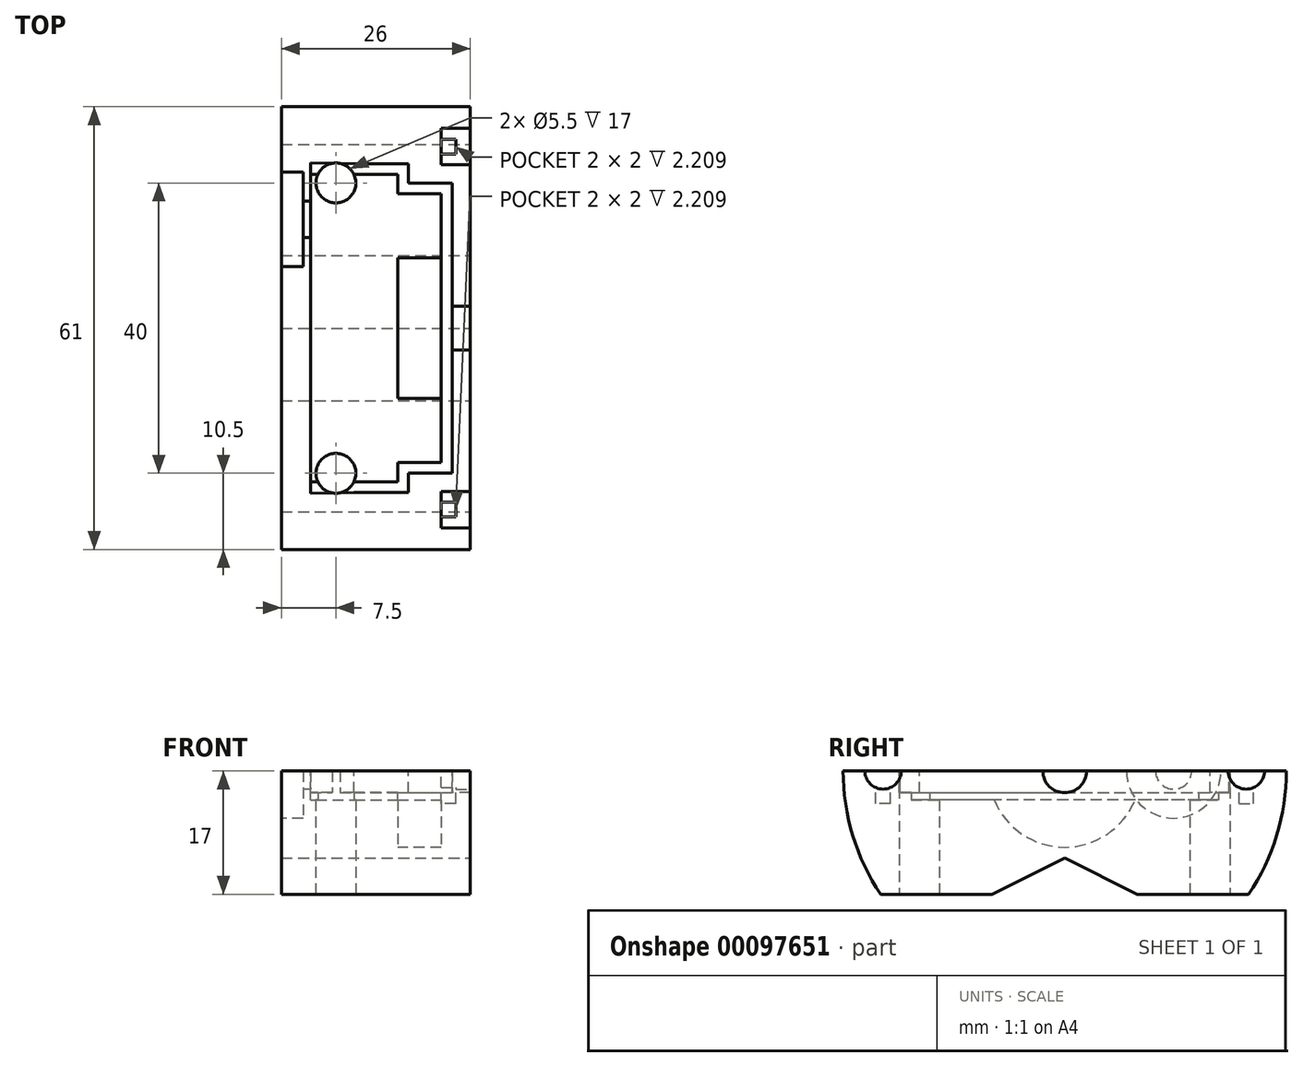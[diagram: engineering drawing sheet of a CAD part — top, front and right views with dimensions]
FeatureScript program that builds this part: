
annotation { "Feature Type Name" : "Feature", "Feature Type Description" : "" }
export const myFeature = defineFeature(function(context is Context, id is Id, definition is map)
    precondition{}
    {
        {
            var Q0;
            Q0=qCreatedBy(makeId("Right.planeOp"),FACE);
            var sketch = newSketch(context, id + "F0", { "sketchPlane" : qUnion([Q0])});
            skArc(sketch, "E0", {"start": v(-30.5, 0) * mm, "mid": v(0, -30.5) * mm, "end": v(30.5, 0) * mm});
            skLineSegment(sketch, "E1.bottom", {"start": v(19.03, -21.15) * mm, "end": v(-19.03, -21.15) * mm});
            skLineSegment(sketch, "E1.left", {"start": v(21.15, -19.03) * mm, "end": v(21.15, 0) * mm});
            skLineSegment(sketch, "E1.right", {"start": v(-21.15, -19.03) * mm, "end": v(-21.15, 0) * mm});
            skLineSegment(sketch, "E2", {"start": v(-30.5, 0) * mm, "end": v(30.5, 0) * mm});
            skPoint(sketch, "E2.endSnap0", {"position": v(21.15, 0) * mm});
            skLineSegment(sketch, "E3", {"start": v(-21.15, -19.03) * mm, "end": v(-19.03, -21.15) * mm});
            skLineSegment(sketch, "E4.MirrorCS", {"start": v(21.15, -19.03) * mm, "end": v(19.03, -21.15) * mm});
            skSolve(sketch);
        }
        {
            var Q0;
            {var subQ0=sQuery(id+"F0.wireOp",EDGE,"E2");var subQ3=sQuery(id+"F0.wireOp",EDGE,"E1.right");var subQ6=makeQuery(id+"F0.imprint","INTERSECT",VERTEX,{"derivedFrom":[subQ3,subQ0]});Q0=makeQuery(id+"F0.imprint","IMPRINT",FACE,{"disambiguationData":[TD([[makeQuery(id+"F0.imprint","IMPRINT",EDGE,{"disambiguationData":[TD([[subQ6,1.0]])],"derivedFrom":subQ3}),1.0]])]});}
            var Q1;
            {var subQ0=sQuery(id+"F0.wireOp",EDGE,"E1.bottom");var subQ5=makeQuery(id+"F0.imprint","INTERSECT",VERTEX,{"derivedFrom":[subQ0,sQuery(id+"F0.wireOp",EDGE,"E3")]});Q1=makeQuery(id+"F0.imprint","IMPRINT",FACE,{"disambiguationData":[TD([[makeQuery(id+"F0.imprint","IMPRINT",EDGE,{"disambiguationData":[TD([[subQ5,1.0]])],"derivedFrom":subQ0}),1.0]])]});}
            var Q2;
            {var subQ0=sQuery(id+"F0.wireOp",EDGE,"E2");var subQ3=sQuery(id+"F0.wireOp",EDGE,"E1.left");var subQ6=makeQuery(id+"F0.imprint","INTERSECT",VERTEX,{"derivedFrom":[subQ3,subQ0]});Q2=makeQuery(id+"F0.imprint","IMPRINT",FACE,{"disambiguationData":[TD([[makeQuery(id+"F0.imprint","IMPRINT",EDGE,{"disambiguationData":[TD([[subQ6,1.0]])],"derivedFrom":subQ3}),-1.0]])]});}
            var Q3;
            {var subQ3=sQuery(id+"F0.wireOp",EDGE,"E4.MirrorCS");Q3=makeQuery(id+"F0.imprint","IMPRINT",FACE,{"disambiguationData":[TD([[makeQuery(id+"F0.imprint","IMPRINT",EDGE,{"derivedFrom":subQ3}),1.0]])]});}
            var Q4;
            {var subQ3=sQuery(id+"F0.wireOp",EDGE,"E3");Q4=makeQuery(id+"F0.imprint","IMPRINT",FACE,{"disambiguationData":[TD([[makeQuery(id+"F0.imprint","IMPRINT",EDGE,{"derivedFrom":subQ3}),-1.0]])]});}
            extrude(context, id + "F1", {"entities" : qUnion([Q0, Q1, Q2, Q3, Q4]), "endBound" : BoundingType.SYMMETRIC, "depth" : 12 * mm});
        }
        {
            var Q0;
            Q0=makeQuery(id+"F1.opExtrude","CAP_FACE",FACE,{"disambiguationData":[OSD([sQuery(id+"F0.wireOp",EDGE,"E0"),sQuery(id+"F0.wireOp",EDGE,"E1.bottom"),sQuery(id+"F0.wireOp",EDGE,"E1.left"),sQuery(id+"F0.wireOp",EDGE,"E1.right"),sQuery(id+"F0.wireOp",EDGE,"E2"),sQuery(id+"F0.wireOp",EDGE,"E3"),sQuery(id+"F0.wireOp",EDGE,"E4.MirrorCS")])],"isStart":false});
            var sketch = newSketch(context, id + "F2", { "sketchPlane" : qUnion([Q0])});
            skArc(sketch, "E5", {"start": v(-30.5, 0) * mm, "mid": v(0, -30.5) * mm, "end": v(30.5, 0) * mm});
            skLineSegment(sketch, "E6", {"start": v(-30.5, 0) * mm, "end": v(30.5, 0) * mm});
            skSolve(sketch);
        }
        {
            var Q0;
            Q0=makeQuery(id+"F2.imprint","IMPRINT",FACE,{"disambiguationData":[TD([[makeQuery(id+"F2.imprint","IMPRINT",EDGE,{"derivedFrom":makeQuery(id+"F1.opExtrude","CAP_EDGE",EDGE,{"disambiguationData":[OSD([sQuery(id+"F0.wireOp",EDGE,"E1.bottom")])],"isStart":false})}),-1.0]])]});
            var Q1;
            {var subQ1=sQuery(id+"F2.wireOp",EDGE,"E5");Q1=makeQuery(id+"F2.imprint","IMPRINT",FACE,{"disambiguationData":[TD([[makeQuery(id+"F2.imprint","IMPRINT",EDGE,{"derivedFrom":subQ1}),1.0]])]});}
            extrude(context, id + "F3", {"entities" : qUnion([Q0, Q1]), "operationType" : NewBodyOperationType.ADD, "depth" : 10 * mm});
        }
        {
            var Q0;
            Q0=makeQuery(id+"F1.opExtrude","CAP_FACE",FACE,{"disambiguationData":[OSD([sQuery(id+"F0.wireOp",EDGE,"E0"),sQuery(id+"F0.wireOp",EDGE,"E1.bottom"),sQuery(id+"F0.wireOp",EDGE,"E1.left"),sQuery(id+"F0.wireOp",EDGE,"E1.right"),sQuery(id+"F0.wireOp",EDGE,"E2"),sQuery(id+"F0.wireOp",EDGE,"E3"),sQuery(id+"F0.wireOp",EDGE,"E4.MirrorCS")])],"isStart":true});
            var sketch = newSketch(context, id + "F4", { "sketchPlane" : qUnion([Q0])});
            skArc(sketch, "E7", {"start": v(-30.5, 0) * mm, "mid": v(0, -30.5) * mm, "end": v(30.5, 0) * mm});
            skLineSegment(sketch, "E8", {"start": v(-30.5, 0) * mm, "end": v(30.5, 0) * mm});
            skSolve(sketch);
        }
        {
            var Q0;
            Q0=makeQuery(id+"F4.imprint","IMPRINT",FACE,{"disambiguationData":[TD([[makeQuery(id+"F4.imprint","IMPRINT",EDGE,{"derivedFrom":makeQuery(id+"F1.opExtrude","CAP_EDGE",EDGE,{"disambiguationData":[OSD([sQuery(id+"F0.wireOp",EDGE,"E1.bottom")])],"isStart":true})}),1.0]])]});
            var Q1;
            {var subQ1=sQuery(id+"F4.wireOp",EDGE,"E7");Q1=makeQuery(id+"F4.imprint","IMPRINT",FACE,{"disambiguationData":[TD([[makeQuery(id+"F4.imprint","IMPRINT",EDGE,{"derivedFrom":subQ1}),-1.0]])]});}
            extrude(context, id + "F5", {"entities" : qUnion([Q0, Q1]), "operationType" : NewBodyOperationType.ADD, "depth" : 4 * mm});
        }
        {
            var Q0;
            {var subQ0=sQuery(id+"F0.wireOp",EDGE,"E2");var subQ1=sQuery(id+"F0.wireOp",EDGE,"E0");Q0=makeQuery(id+"F5.boolean.opBoolean","MERGE",FACE,{"derivedFrom":[makeQuery(id+"F3.boolean.opBoolean","MERGE",FACE,{"derivedFrom":[makeQuery(id+"F1.opExtrude","SWEPT_FACE",FACE,{"disambiguationData":[OSD([subQ0]),TDD([makeQuery(id+"F0.imprint","IMPRINT",EDGE,{"disambiguationData":[TD([[makeQuery(id+"F0.imprint","INTERSECT",VERTEX,{"disambiguationData":[OD(0.0)],"derivedFrom":[subQ1,subQ0]}),-1.0]])],"derivedFrom":subQ0})])]}),makeQuery(id+"F1.opExtrude","SWEPT_FACE",FACE,{"disambiguationData":[OSD([subQ0]),TDD([makeQuery(id+"F0.imprint","IMPRINT",EDGE,{"disambiguationData":[TD([[makeQuery(id+"F0.imprint","INTERSECT",VERTEX,{"disambiguationData":[OD(1.0)],"derivedFrom":[subQ1,subQ0]}),1.0]])],"derivedFrom":subQ0})])]}),makeQuery(id+"F3.opExtrude","SWEPT_FACE",FACE,{"disambiguationData":[OSD([sQuery(id+"F2.wireOp",EDGE,"E6")])]})]}),makeQuery(id+"F5.opExtrude","SWEPT_FACE",FACE,{"disambiguationData":[OSD([sQuery(id+"F4.wireOp",EDGE,"E8")])]})]});}
            var sketch = newSketch(context, id + "F6", { "sketchPlane" : qUnion([Q0])});
            skLineSegment(sketch, "E9.bottom", {"start": v(6, 0) * mm, "end": v(12, 0) * mm});
            skLineSegment(sketch, "E9.top", {"start": v(6, 10.5) * mm, "end": v(12, 10.5) * mm});
            skLineSegment(sketch, "E9.left", {"start": v(6, 0) * mm, "end": v(6, 10.5) * mm});
            skLineSegment(sketch, "E9.right", {"start": v(12, 0) * mm, "end": v(12, 10.5) * mm});
            skLineSegment(sketch, "E10.bottom", {"start": v(16, 0) * mm, "end": v(12, 0) * mm});
            skLineSegment(sketch, "E10.top", {"start": v(16, 3) * mm, "end": v(12, 3) * mm});
            skLineSegment(sketch, "E10.left", {"start": v(16, 0) * mm, "end": v(16, 3) * mm});
            skLineSegment(sketch, "E10.right", {"start": v(12, 0) * mm, "end": v(12, 3) * mm});
            skLineSegment(sketch, "E11.bottom", {"start": v(12, -22.5) * mm, "end": v(16, -22.5) * mm});
            skLineSegment(sketch, "E11.top", {"start": v(12, -27.5) * mm, "end": v(16, -27.5) * mm});
            skLineSegment(sketch, "E11.left", {"start": v(12, -22.5) * mm, "end": v(12, -27.5) * mm});
            skLineSegment(sketch, "E11.right", {"start": v(16, -22.5) * mm, "end": v(16, -27.5) * mm});
            skLineSegment(sketch, "E12.MirrorCS", {"start": v(12, 22.5) * mm, "end": v(12, 27.5) * mm});
            skLineSegment(sketch, "E13.MirrorCS", {"start": v(12, 22.5) * mm, "end": v(16, 22.5) * mm});
            skLineSegment(sketch, "E14.MirrorCS", {"start": v(12, 27.5) * mm, "end": v(16, 27.5) * mm});
            skLineSegment(sketch, "E15.MirrorCS", {"start": v(16, 22.5) * mm, "end": v(16, 27.5) * mm});
            skLineSegment(sketch, "E16", {"start": v(12, -25) * mm, "end": v(16, -25) * mm});
            skLineSegment(sketch, "E17.MirrorCS", {"start": v(12, 25) * mm, "end": v(16, 25) * mm});
            skSolve(sketch);
        }
        {
            var Q0;
            Q0=makeQuery(id+"F6.imprint","IMPRINT",FACE,{"disambiguationData":[TD([[makeQuery(id+"F6.imprint","IMPRINT",EDGE,{"derivedFrom":sQuery(id+"F6.wireOp",EDGE,"E9.bottom")}),1.0]])]});
            var Q1;
            Q1=makeQuery(id+"F6.imprint","IMPRINT",FACE,{"disambiguationData":[TD([[makeQuery(id+"F6.imprint","IMPRINT",EDGE,{"derivedFrom":sQuery(id+"F6.wireOp",EDGE,"E10.bottom")}),-1.0]])]});
            var Q2;
            Q2=sQuery(id+"F6.wireOp",EDGE,"E9.bottom");
            revolve(context, id + "F7", {"operationType" : NewBodyOperationType.REMOVE, "entities" : qUnion([Q0, Q1]), "axis" : qUnion([Q2]), "revolveType" : RevolveType.FULL});
        }
        {
            var Q0;
            {var subQ0=sQuery(id+"F6.wireOp",EDGE,"E11.top");Q0=makeQuery(id+"F6.imprint","IMPRINT",FACE,{"disambiguationData":[TD([[makeQuery(id+"F6.imprint","IMPRINT",EDGE,{"derivedFrom":subQ0}),1.0]])]});}
            var Q1;
            Q1=sQuery(id+"F6.wireOp",EDGE,"E16");
            revolve(context, id + "F8", {"operationType" : NewBodyOperationType.REMOVE, "entities" : qUnion([Q0]), "axis" : qUnion([Q1]), "revolveType" : RevolveType.FULL, "oppositeDirection" : true});
        }
        {
            var Q0;
            {var subQ0=sQuery(id+"F6.wireOp",EDGE,"E13.MirrorCS");Q0=makeQuery(id+"F6.imprint","IMPRINT",FACE,{"disambiguationData":[TD([[makeQuery(id+"F6.imprint","IMPRINT",EDGE,{"derivedFrom":subQ0}),1.0]])]});}
            var Q1;
            Q1=sQuery(id+"F6.wireOp",EDGE,"E17.MirrorCS");
            revolve(context, id + "F9", {"operationType" : NewBodyOperationType.REMOVE, "entities" : qUnion([Q0]), "axis" : qUnion([Q1]), "revolveType" : RevolveType.FULL, "oppositeDirection" : true});
        }
        {
            var Q0;
            {var subQ16=sQuery(id+"F6.wireOp",EDGE,"E9.bottom");Q0=makeQuery(id+"F6.imprint","IMPRINT",FACE,{"disambiguationData":[TD([[makeQuery(id+"F6.imprint","IMPRINT",EDGE,{"derivedFrom":subQ16}),-1.0]])]});}
            var sketch = newSketch(context, id + "F10", { "sketchPlane" : qUnion([Q0])});
            skLineSegment(sketch, "E18.bottom", {"start": v(14, -26) * mm, "end": v(12, -26) * mm});
            skLineSegment(sketch, "E18.top", {"start": v(14, -24) * mm, "end": v(12, -24) * mm});
            skLineSegment(sketch, "E18.left", {"start": v(14, -26) * mm, "end": v(14, -24) * mm});
            skPoint(sketch, "E18.middle", {"position": v(12, -25) * mm});
            skLineSegment(sketch, "E19", {"start": v(12, -24) * mm, "end": v(12, -26) * mm});
            skPoint(sketch, "E18.right.end.orphan", {"position": v(10, -24) * mm});
            skPoint(sketch, "E20.orphan", {"position": v(10, -26) * mm});
            skLineSegment(sketch, "E21.MirrorCS", {"start": v(14, 24) * mm, "end": v(12, 24) * mm});
            skLineSegment(sketch, "E22.MirrorCS", {"start": v(14, 26) * mm, "end": v(14, 24) * mm});
            skLineSegment(sketch, "E23.MirrorCS", {"start": v(14, 26) * mm, "end": v(12, 26) * mm});
            skLineSegment(sketch, "E24.MirrorCS", {"start": v(12, 24) * mm, "end": v(12, 26) * mm});
            skSolve(sketch);
        }
        {
            var Q0;
            {var subQ5=sQuery(id+"F10.wireOp",EDGE,"E18.bottom");Q0=makeQuery(id+"F10.imprint","IMPRINT",FACE,{"disambiguationData":[TD([[makeQuery(id+"F10.imprint","IMPRINT",EDGE,{"derivedFrom":subQ5}),-1.0]])]});}
            var Q1;
            {var subQ2=sQuery(id+"F10.wireOp",EDGE,"E21.MirrorCS");Q1=makeQuery(id+"F10.imprint","IMPRINT",FACE,{"disambiguationData":[TD([[makeQuery(id+"F10.imprint","IMPRINT",EDGE,{"derivedFrom":subQ2}),-1.0]])]});}
            extrude(context, id + "F11", {"entities" : qUnion([Q0, Q1]), "operationType" : NewBodyOperationType.REMOVE, "oppositeDirection" : true, "depth" : 4.5 * mm});
        }
        {
            var Q0;
            {var subQ0=sQuery(id+"F0.wireOp",EDGE,"E2");var subQ1=sQuery(id+"F0.wireOp",EDGE,"E0");Q0=makeQuery(id+"F5.boolean.opBoolean","MERGE",FACE,{"derivedFrom":[makeQuery(id+"F3.boolean.opBoolean","MERGE",FACE,{"derivedFrom":[makeQuery(id+"F1.opExtrude","SWEPT_FACE",FACE,{"disambiguationData":[OSD([subQ0]),TDD([makeQuery(id+"F0.imprint","IMPRINT",EDGE,{"disambiguationData":[TD([[makeQuery(id+"F0.imprint","INTERSECT",VERTEX,{"disambiguationData":[OD(0.0)],"derivedFrom":[subQ1,subQ0]}),-1.0]])],"derivedFrom":subQ0})])]}),makeQuery(id+"F1.opExtrude","SWEPT_FACE",FACE,{"disambiguationData":[OSD([subQ0]),TDD([makeQuery(id+"F0.imprint","IMPRINT",EDGE,{"disambiguationData":[TD([[makeQuery(id+"F0.imprint","INTERSECT",VERTEX,{"disambiguationData":[OD(1.0)],"derivedFrom":[subQ1,subQ0]}),1.0]])],"derivedFrom":subQ0})])]}),makeQuery(id+"F3.opExtrude","SWEPT_FACE",FACE,{"disambiguationData":[OSD([sQuery(id+"F2.wireOp",EDGE,"E6")])]})]}),makeQuery(id+"F5.opExtrude","SWEPT_FACE",FACE,{"disambiguationData":[OSD([sQuery(id+"F4.wireOp",EDGE,"E8")])]})]});}
            var sketch = newSketch(context, id + "F12", { "sketchPlane" : qUnion([Q0])});
            skLineSegment(sketch, "E25.bottom", {"start": v(6, 18.5) * mm, "end": v(12, 18.5) * mm});
            skLineSegment(sketch, "E25.top", {"start": v(6, -18.5) * mm, "end": v(12, -18.5) * mm});
            skLineSegment(sketch, "E25.left", {"start": v(6, 18.5) * mm, "end": v(6, -18.5) * mm});
            skLineSegment(sketch, "E25.right", {"start": v(12, 18.5) * mm, "end": v(12, -18.5) * mm});
            skPoint(sketch, "E26", {"position": v(9, 15.5) * mm});
            skPoint(sketch, "E27.MirrorP", {"position": v(9, -15.5) * mm});
            skSolve(sketch);
        }
        {
            var Q0;
            {var subQ7=sQuery(id+"F12.wireOp",EDGE,"E25.bottom");Q0=makeQuery(id+"F12.imprint","IMPRINT",FACE,{"disambiguationData":[TD([[makeQuery(id+"F12.imprint","IMPRINT",EDGE,{"derivedFrom":subQ7}),-1.0]])]});}
            var Q1;
            {var subQ4=sQuery(id+"F12.wireOp",EDGE,"E25.top");Q1=makeQuery(id+"F12.imprint","IMPRINT",FACE,{"disambiguationData":[TD([[makeQuery(id+"F12.imprint","IMPRINT",EDGE,{"derivedFrom":subQ4}),1.0]])]});}
            var Q2;
            {var subQ0=sQuery(id+"F12.wireOp",EDGE,"E25.left");var subQ1=makeQuery(id+"F7.opRevolve","SWEPT_FACE",FACE,{"disambiguationData":[OSD([sQuery(id+"F6.wireOp",EDGE,"E9.top")])]});var subQ2=sQuery(id+"F0.wireOp",EDGE,"E2");var subQ3=sQuery(id+"F0.wireOp",EDGE,"E0");var subQ4=makeQuery(id+"F5.boolean.opBoolean","MERGE",FACE,{"derivedFrom":[makeQuery(id+"F3.boolean.opBoolean","MERGE",FACE,{"derivedFrom":[makeQuery(id+"F1.opExtrude","SWEPT_FACE",FACE,{"disambiguationData":[OSD([subQ2]),TDD([makeQuery(id+"F0.imprint","IMPRINT",EDGE,{"disambiguationData":[TD([[makeQuery(id+"F0.imprint","INTERSECT",VERTEX,{"disambiguationData":[OD(0.0)],"derivedFrom":[subQ3,subQ2]}),-1.0]])],"derivedFrom":subQ2})])]}),makeQuery(id+"F1.opExtrude","SWEPT_FACE",FACE,{"disambiguationData":[OSD([subQ2]),TDD([makeQuery(id+"F0.imprint","IMPRINT",EDGE,{"disambiguationData":[TD([[makeQuery(id+"F0.imprint","INTERSECT",VERTEX,{"disambiguationData":[OD(1.0)],"derivedFrom":[subQ3,subQ2]}),1.0]])],"derivedFrom":subQ2})])]}),makeQuery(id+"F3.opExtrude","SWEPT_FACE",FACE,{"disambiguationData":[OSD([sQuery(id+"F2.wireOp",EDGE,"E6")])]})]}),makeQuery(id+"F5.opExtrude","SWEPT_FACE",FACE,{"disambiguationData":[OSD([sQuery(id+"F4.wireOp",EDGE,"E8")])]})]});var subQ5=makeQuery(id+"F7.boolean.opBoolean","INTERSECT",EDGE,{"disambiguationData":[OD(0.0)],"derivedFrom":[subQ4,subQ1]});var subQ6=makeQuery(id+"F12.imprint","INTERSECT",VERTEX,{"derivedFrom":[subQ5,subQ0]});var subQ7=makeQuery(id+"F7.boolean.opBoolean","INTERSECT",EDGE,{"disambiguationData":[OD(1.0)],"derivedFrom":[subQ4,subQ1]});var subQ8=makeQuery(id+"F12.imprint","INTERSECT",VERTEX,{"derivedFrom":[subQ7,subQ0]});Q2=makeQuery(id+"F12.imprint","IMPRINT",FACE,{"disambiguationData":[TD([[makeQuery(id+"F12.imprint","IMPRINT",EDGE,{"disambiguationData":[TD([[subQ6,-1.0],[subQ8,1.0]])],"derivedFrom":subQ0}),1.0]])]});}
            extrude(context, id + "F13", {"entities" : qUnion([Q0, Q1, Q2]), "operationType" : NewBodyOperationType.REMOVE, "oppositeDirection" : true, "depth" : 4 * mm});
        }
        {
            var Q0;
            Q0=makeQuery(id+"F3.opExtrude","CAP_FACE",FACE,{"disambiguationData":[OSD([sQuery(id+"F2.wireOp",EDGE,"E5"),sQuery(id+"F2.wireOp",EDGE,"E6")])],"isStart":false});
            var sketch = newSketch(context, id + "F14", { "sketchPlane" : qUnion([Q0])});
            skLineSegment(sketch, "E28", {"start": v(25.32, -17) * mm, "end": v(10, -17) * mm});
            skLineSegment(sketch, "E29", {"start": v(10, -17) * mm, "end": v(0, -12) * mm});
            skLineSegment(sketch, "E30.MirrorCS", {"start": v(-10, -17) * mm, "end": v(0, -12) * mm});
            skLineSegment(sketch, "E31.trimOffspring", {"start": v(-10, -17) * mm, "end": v(-25.32, -17) * mm});
            skArc(sketch, "E32", {"start": v(-25.32, -17) * mm, "mid": v(0, -30.5) * mm, "end": v(25.32, -17) * mm});
            skSolve(sketch);
        }
        {
            var Q0;
            Q0=makeQuery(id+"F13.boolean.opBoolean","COPY",FACE,{"disambiguationData":[OD(0.0)],"derivedFrom":makeQuery(id+"F13.opExtrude","CAP_FACE",FACE,{"disambiguationData":[OSD([sQuery(id+"F12.wireOp",EDGE,"E25.bottom"),sQuery(id+"F12.wireOp",EDGE,"E25.top"),sQuery(id+"F12.wireOp",EDGE,"E25.left"),sQuery(id+"F12.wireOp",EDGE,"E25.right")])],"isStart":false})});
            var sketch = newSketch(context, id + "F15", { "sketchPlane" : qUnion([Q0])});
            skLineSegment(sketch, "E33.bottom", {"start": v(-6, 21.15) * mm, "end": v(6, 21.15) * mm});
            skLineSegment(sketch, "E33.top", {"start": v(-6, -21.15) * mm, "end": v(6, -21.15) * mm});
            skLineSegment(sketch, "E33.left", {"start": v(-6, 21.15) * mm, "end": v(-6, -21.15) * mm});
            skLineSegment(sketch, "E33.right", {"start": v(6, 21.15) * mm, "end": v(6, -21.15) * mm});
            skSolve(sketch);
        }
        {
            var Q0;
            {var subQ3=sQuery(id+"F15.wireOp",EDGE,"E33.bottom");Q0=makeQuery(id+"F15.imprint","IMPRINT",FACE,{"disambiguationData":[TD([[makeQuery(id+"F15.imprint","IMPRINT",EDGE,{"derivedFrom":subQ3}),-1.0]])]});}
            extrude(context, id + "F16", {"entities" : qUnion([Q0]), "operationType" : NewBodyOperationType.ADD, "endBound" : BoundingType.UP_TO_NEXT, "oppositeDirection" : true, "depth" : 25 * mm});
        }
        {
            var Q0;
            Q0=makeQuery(id+"F14.imprint","IMPRINT",FACE,{"disambiguationData":[TD([[makeQuery(id+"F14.imprint","IMPRINT",EDGE,{"derivedFrom":sQuery(id+"F14.wireOp",EDGE,"E28")}),1.0]])]});
            extrude(context, id + "F17", {"entities" : qUnion([Q0]), "operationType" : NewBodyOperationType.REMOVE, "endBound" : BoundingType.UP_TO_NEXT, "oppositeDirection" : true, "depth" : 25 * mm});
        }
        {
            var Q0;
            Q0=makeQuery(id+"F17.boolean.opBoolean","COPY",FACE,{"derivedFrom":makeQuery(id+"F17.opExtrude","SWEPT_FACE",FACE,{"disambiguationData":[OSD([sQuery(id+"F14.wireOp",EDGE,"E28")])]})});
            var sketch = newSketch(context, id + "F18", { "sketchPlane" : qUnion([Q0])});
            skPoint(sketch, "E34", {"position": v(-2.5, -20) * mm});
            skPoint(sketch, "E35.MirrorP", {"position": v(-2.5, 20) * mm});
            skSolve(sketch);
        }
        {
            var Q0;
            Q0=sQuery(id+"F18.wireOp",VERTEX,"E34");
            var Q1;
            Q1=sQuery(id+"F18.wireOp",VERTEX,"E35.MirrorP");
            var Q2;
            Q2=makeQuery(id+"F1.opExtrude","SWEPT_BODY",BODY,{"disambiguationData":[OSD([sQuery(id+"F0.wireOp",EDGE,"E0"),sQuery(id+"F0.wireOp",EDGE,"E1.bottom"),sQuery(id+"F0.wireOp",EDGE,"E1.left"),sQuery(id+"F0.wireOp",EDGE,"E1.right"),sQuery(id+"F0.wireOp",EDGE,"E2"),sQuery(id+"F0.wireOp",EDGE,"E3"),sQuery(id+"F0.wireOp",EDGE,"E4.MirrorCS")])]});
            hole(context, id + "F19", {"style" : HoleStyle.SIMPLE, "endStyle" : HoleEndStyle.THROUGH, "standardTappedOrClearance" : lookupTablePath({ "standard" : "ISO", "fit" : "Normal", "size" : "M5", "type" : "Clearance" }), "standardBlindInLast" : lookupTablePath({ "fit" : "Standard", "standard" : "ISO", "size" : "M5", "type" : "Clearance" }), "holeDiameter" : 5.5 * mm, "locations" : qUnion([Q0, Q1]), "scope" : qUnion([Q2]), "isTappedThrough" : true});
        }
        {
            var Q0;
            Q0=makeQuery(id+"F5.opExtrude","CAP_FACE",FACE,{"disambiguationData":[OSD([sQuery(id+"F4.wireOp",EDGE,"E7"),sQuery(id+"F4.wireOp",EDGE,"E8")])],"isStart":false});
            var sketch = newSketch(context, id + "F20", { "sketchPlane" : qUnion([Q0])});
            skCircle(sketch, "E36", {"center": v(-15, 0) * mm, "radius": 6.5 * mm});
            skCircle(sketch, "E37", {"center": v(-15, 0) * mm, "radius": 2.5 * mm});
            skCircle(sketch, "E38.MirrorC", {"center": v(15, 0) * mm, "radius": 6.5 * mm});
            skCircle(sketch, "E39.MirrorC", {"center": v(15, 0) * mm, "radius": 2.5 * mm});
            skSolve(sketch);
        }
        {
            var Q0;
            {var subQ0=sQuery(id+"F20.wireOp",EDGE,"E36");var subQ1=makeQuery(id+"F5.opExtrude","CAP_EDGE",EDGE,{"disambiguationData":[OSD([sQuery(id+"F4.wireOp",EDGE,"E8")])],"isStart":false});var subQ2=makeQuery(id+"F20.imprint","INTERSECT",VERTEX,{"disambiguationData":[OD(0.0)],"derivedFrom":[subQ1,subQ0]});Q0=makeQuery(id+"F20.imprint","IMPRINT",FACE,{"disambiguationData":[TD([[makeQuery(id+"F20.imprint","IMPRINT",EDGE,{"disambiguationData":[TD([[subQ2,-1.0]])],"derivedFrom":subQ0}),1.0]])]});}
            var Q1;
            {var subQ0=sQuery(id+"F20.wireOp",EDGE,"E37");var subQ1=makeQuery(id+"F5.opExtrude","CAP_EDGE",EDGE,{"disambiguationData":[OSD([sQuery(id+"F4.wireOp",EDGE,"E8")])],"isStart":false});var subQ2=makeQuery(id+"F20.imprint","INTERSECT",VERTEX,{"disambiguationData":[OD(0.0)],"derivedFrom":[subQ1,subQ0]});Q1=makeQuery(id+"F20.imprint","IMPRINT",FACE,{"disambiguationData":[TD([[makeQuery(id+"F20.imprint","IMPRINT",EDGE,{"disambiguationData":[TD([[subQ2,-1.0]])],"derivedFrom":subQ0}),1.0]])]});}
            var Q2;
            {var subQ0=sQuery(id+"F20.wireOp",EDGE,"E38.MirrorC");var subQ1=makeQuery(id+"F5.opExtrude","CAP_EDGE",EDGE,{"disambiguationData":[OSD([sQuery(id+"F4.wireOp",EDGE,"E8")])],"isStart":false});var subQ2=makeQuery(id+"F20.imprint","INTERSECT",VERTEX,{"disambiguationData":[OD(0.0)],"derivedFrom":[subQ1,subQ0]});Q2=makeQuery(id+"F20.imprint","IMPRINT",FACE,{"disambiguationData":[TD([[makeQuery(id+"F20.imprint","IMPRINT",EDGE,{"disambiguationData":[TD([[subQ2,-1.0]])],"derivedFrom":subQ0}),-1.0]])]});}
            var Q3;
            {var subQ0=sQuery(id+"F20.wireOp",EDGE,"E39.MirrorC");var subQ1=makeQuery(id+"F5.opExtrude","CAP_EDGE",EDGE,{"disambiguationData":[OSD([sQuery(id+"F4.wireOp",EDGE,"E8")])],"isStart":false});var subQ2=makeQuery(id+"F20.imprint","INTERSECT",VERTEX,{"disambiguationData":[OD(0.0)],"derivedFrom":[subQ1,subQ0]});Q3=makeQuery(id+"F20.imprint","IMPRINT",FACE,{"disambiguationData":[TD([[makeQuery(id+"F20.imprint","IMPRINT",EDGE,{"disambiguationData":[TD([[subQ2,-1.0]])],"derivedFrom":subQ0}),-1.0]])]});}
            extrude(context, id + "F21", {"entities" : qUnion([Q0, Q1, Q2, Q3]), "operationType" : NewBodyOperationType.REMOVE, "oppositeDirection" : true, "depth" : 3 * mm});
        }
        {
            var Q0;
            {var subQ0=sQuery(id+"F20.wireOp",EDGE,"E37");var subQ1=makeQuery(id+"F5.opExtrude","CAP_EDGE",EDGE,{"disambiguationData":[OSD([sQuery(id+"F4.wireOp",EDGE,"E8")])],"isStart":false});var subQ2=makeQuery(id+"F20.imprint","INTERSECT",VERTEX,{"disambiguationData":[OD(0.0)],"derivedFrom":[subQ1,subQ0]});Q0=makeQuery(id+"F20.imprint","IMPRINT",FACE,{"disambiguationData":[TD([[makeQuery(id+"F20.imprint","IMPRINT",EDGE,{"disambiguationData":[TD([[subQ2,-1.0]])],"derivedFrom":subQ0}),1.0]])]});}
            var Q1;
            {var subQ0=sQuery(id+"F20.wireOp",EDGE,"E39.MirrorC");var subQ1=makeQuery(id+"F5.opExtrude","CAP_EDGE",EDGE,{"disambiguationData":[OSD([sQuery(id+"F4.wireOp",EDGE,"E8")])],"isStart":false});var subQ2=makeQuery(id+"F20.imprint","INTERSECT",VERTEX,{"disambiguationData":[OD(0.0)],"derivedFrom":[subQ1,subQ0]});Q1=makeQuery(id+"F20.imprint","IMPRINT",FACE,{"disambiguationData":[TD([[makeQuery(id+"F20.imprint","IMPRINT",EDGE,{"disambiguationData":[TD([[subQ2,-1.0]])],"derivedFrom":subQ0}),-1.0]])]});}
            extrude(context, id + "F22", {"entities" : qUnion([Q0, Q1]), "operationType" : NewBodyOperationType.REMOVE, "oppositeDirection" : true, "depth" : 4 * mm});
        }
        {
            var Q0;
            {var subQ0=sQuery(id+"F4.wireOp",EDGE,"E8");var subQ1=sQuery(id+"F4.wireOp",EDGE,"E7");var subQ2=sQuery(id+"F2.wireOp",EDGE,"E6");var subQ3=sQuery(id+"F2.wireOp",EDGE,"E5");var subQ4=sQuery(id+"F0.wireOp",EDGE,"E0");var subQ5=sQuery(id+"F20.wireOp",EDGE,"E36");var subQ6=sQuery(id+"F0.wireOp",EDGE,"E1.left");var subQ7=sQuery(id+"F0.wireOp",EDGE,"E2");Q0=makeQuery(id+"F22.boolean.opBoolean","SPLIT",FACE,{"disambiguationData":[TD([makeQuery(id+"F1.opExtrude","SWEPT_FACE",FACE,{"disambiguationData":[OSD([subQ4])]}),makeQuery(id+"F1.opExtrude","SWEPT_FACE",FACE,{"disambiguationData":[OSD([subQ6])]}),makeQuery(id+"F3.opExtrude","SWEPT_FACE",FACE,{"disambiguationData":[OSD([subQ3])]}),makeQuery(id+"F3.opExtrude","CAP_FACE",FACE,{"disambiguationData":[OSD([subQ3,subQ2])],"isStart":true}),makeQuery(id+"F3.opExtrude","CAP_FACE",FACE,{"disambiguationData":[OSD([subQ3,subQ2])],"isStart":false}),makeQuery(id+"F5.opExtrude","SWEPT_FACE",FACE,{"disambiguationData":[OSD([subQ1])]}),makeQuery(id+"F5.opExtrude","CAP_FACE",FACE,{"disambiguationData":[OSD([subQ1,subQ0])],"isStart":true}),makeQuery(id+"F5.opExtrude","CAP_FACE",FACE,{"disambiguationData":[OSD([subQ1,subQ0])],"isStart":false}),makeQuery(id+"F7.boolean.opBoolean","COPY",FACE,{"derivedFrom":makeQuery(id+"F7.opRevolve","SWEPT_FACE",FACE,{"disambiguationData":[OSD([sQuery(id+"F6.wireOp",EDGE,"E9.right")])]})}),makeQuery(id+"F7.boolean.opBoolean","COPY",FACE,{"derivedFrom":makeQuery(id+"F7.opRevolve","SWEPT_FACE",FACE,{"disambiguationData":[OSD([sQuery(id+"F6.wireOp",EDGE,"E10.top")])]})}),makeQuery(id+"F9.boolean.opBoolean","COPY",FACE,{"derivedFrom":makeQuery(id+"F9.opRevolve","SWEPT_FACE",FACE,{"disambiguationData":[OSD([sQuery(id+"F6.wireOp",EDGE,"E12.MirrorCS")])]})}),makeQuery(id+"F9.boolean.opBoolean","COPY",FACE,{"derivedFrom":makeQuery(id+"F9.opRevolve","SWEPT_FACE",FACE,{"disambiguationData":[OSD([sQuery(id+"F6.wireOp",EDGE,"E13.MirrorCS")])]})}),makeQuery(id+"F11.opExtrude","SWEPT_FACE",FACE,{"disambiguationData":[OSD([sQuery(id+"F10.wireOp",EDGE,"E24.MirrorCS")])]}),makeQuery(id+"F13.opExtrude","SWEPT_FACE",FACE,{"disambiguationData":[OSD([sQuery(id+"F12.wireOp",EDGE,"E25.right")])]}),makeQuery(id+"F13.boolean.opBoolean","COPY",FACE,{"derivedFrom":makeQuery(id+"F13.opExtrude","SWEPT_FACE",FACE,{"disambiguationData":[OSD([sQuery(id+"F12.wireOp",EDGE,"E25.bottom")])]})}),makeQuery(id+"F19.hole-0.boolean.opBoolean","COPY",FACE,{"derivedFrom":makeQuery(id+"F19.hole-0.opRevolve","SWEPT_FACE",FACE,{"disambiguationData":[OSD([sQuery(id+"F19.hole-0.sketch.wireOp",EDGE,"core_line_2")])]})}),makeQuery(id+"F21.boolean.opBoolean","COPY",FACE,{"derivedFrom":makeQuery(id+"F21.opExtrude","SWEPT_FACE",FACE,{"disambiguationData":[OSD([subQ5])]})}),makeQuery(id+"F21.boolean.opBoolean","COPY",FACE,{"derivedFrom":makeQuery(id+"F21.opExtrude","CAP_FACE",FACE,{"disambiguationData":[OSD([subQ0,subQ5])],"isStart":false})}),makeQuery(id+"F22.opExtrude","SWEPT_FACE",FACE,{"disambiguationData":[OSD([sQuery(id+"F20.wireOp",EDGE,"E37")])]})])],"derivedFrom":makeQuery(id+"F5.boolean.opBoolean","MERGE",FACE,{"derivedFrom":[makeQuery(id+"F3.boolean.opBoolean","MERGE",FACE,{"derivedFrom":[makeQuery(id+"F1.opExtrude","SWEPT_FACE",FACE,{"disambiguationData":[OSD([subQ7]),TDD([makeQuery(id+"F0.imprint","IMPRINT",EDGE,{"disambiguationData":[TD([[makeQuery(id+"F0.imprint","INTERSECT",VERTEX,{"disambiguationData":[OD(0.0)],"derivedFrom":[subQ4,subQ7]}),-1.0]])],"derivedFrom":subQ7})])]}),makeQuery(id+"F1.opExtrude","SWEPT_FACE",FACE,{"disambiguationData":[OSD([subQ7]),TDD([makeQuery(id+"F0.imprint","IMPRINT",EDGE,{"disambiguationData":[TD([[makeQuery(id+"F0.imprint","INTERSECT",VERTEX,{"disambiguationData":[OD(1.0)],"derivedFrom":[subQ4,subQ7]}),1.0]])],"derivedFrom":subQ7})])]}),makeQuery(id+"F3.opExtrude","SWEPT_FACE",FACE,{"disambiguationData":[OSD([subQ2])]})]}),makeQuery(id+"F5.opExtrude","SWEPT_FACE",FACE,{"disambiguationData":[OSD([subQ0])]})]})});}
            var sketch = newSketch(context, id + "F23", { "sketchPlane" : qUnion([Q0])});
            skLineSegment(sketch, "E40.0", {"start": v(6, 21.15) * mm, "end": v(0, 21.15) * mm});
            skLineSegment(sketch, "E41.0", {"start": v(6, 18.5) * mm, "end": v(6, 21.15) * mm});
            skLineSegment(sketch, "E42.0", {"start": v(6, 18.5) * mm, "end": v(12, 18.5) * mm});
            skLineSegment(sketch, "E43.0", {"start": v(12, 18.5) * mm, "end": v(12, 3) * mm});
            skLineSegment(sketch, "E44.0", {"start": v(12, -3) * mm, "end": v(12, -18.5) * mm});
            skLineSegment(sketch, "E45.0", {"start": v(6, -18.5) * mm, "end": v(12, -18.5) * mm});
            skLineSegment(sketch, "E46.0", {"start": v(6, -21.15) * mm, "end": v(6, -18.5) * mm});
            skLineSegment(sketch, "E47.0", {"start": v(6, -21.15) * mm, "end": v(0, -21.15) * mm});
            skLineSegment(sketch, "E48", {"start": v(0, 22.65) * mm, "end": v(7.5, 22.65) * mm});
            skLineSegment(sketch, "E49", {"start": v(7.5, 22.65) * mm, "end": v(7.5, 20) * mm});
            skLineSegment(sketch, "E50", {"start": v(7.5, 20) * mm, "end": v(13.5, 20) * mm});
            skLineSegment(sketch, "E51", {"start": v(13.5, 20) * mm, "end": v(13.5, 3) * mm});
            skLineSegment(sketch, "E52.MirrorCS", {"start": v(0, -22.65) * mm, "end": v(7.5, -22.65) * mm});
            skLineSegment(sketch, "E53.MirrorCS", {"start": v(7.5, -22.65) * mm, "end": v(7.5, -20) * mm});
            skLineSegment(sketch, "E54.MirrorCS", {"start": v(7.5, -20) * mm, "end": v(13.5, -20) * mm});
            skLineSegment(sketch, "E55.MirrorCS", {"start": v(13.5, -20) * mm, "end": v(13.5, -3) * mm});
            skLineSegment(sketch, "E56", {"start": v(13.5, -3) * mm, "end": v(13.5, 3) * mm});
            skLineSegment(sketch, "E57", {"start": v(12, -3) * mm, "end": v(12, 3) * mm});
            skPoint(sketch, "E58.MirrorCS.end.orphan", {"position": v(12, -3) * mm});
            skPoint(sketch, "E58.MirrorCS.start.orphan", {"position": v(13.5, -3) * mm});
            skLineSegment(sketch, "E59", {"start": v(0, 21.15) * mm, "end": v(-6, 21.15) * mm});
            skLineSegment(sketch, "E60", {"start": v(-6, 21.15) * mm, "end": v(-6, 22.75) * mm});
            skPoint(sketch, "E60.endSnap0", {"position": v(-2.5, 22.75) * mm});
            skLineSegment(sketch, "E61", {"start": v(-6, 22.75) * mm, "end": v(0, 22.65) * mm});
            skLineSegment(sketch, "E62.MirrorCS", {"start": v(0, -21.15) * mm, "end": v(-6, -21.15) * mm});
            skLineSegment(sketch, "E63.MirrorCS", {"start": v(-6, -22.75) * mm, "end": v(0, -22.65) * mm});
            skLineSegment(sketch, "E64.MirrorCS", {"start": v(-6, -21.15) * mm, "end": v(-6, -22.75) * mm});
            skPoint(sketch, "E65.MirrorCS.end.orphan", {"position": v(0, -22.65) * mm});
            skPoint(sketch, "E65.MirrorCS.start.orphan", {"position": v(0, -21.15) * mm});
            skSolve(sketch);
        }
        {
            var Q0;
            Q0 = qSketchRegion(id + "F23", true);
            extrude(context, id + "F24", {"entities" : qUnion([Q0]), "operationType" : NewBodyOperationType.REMOVE, "oppositeDirection" : true, "depth" : 3 * mm});
        }
    });
